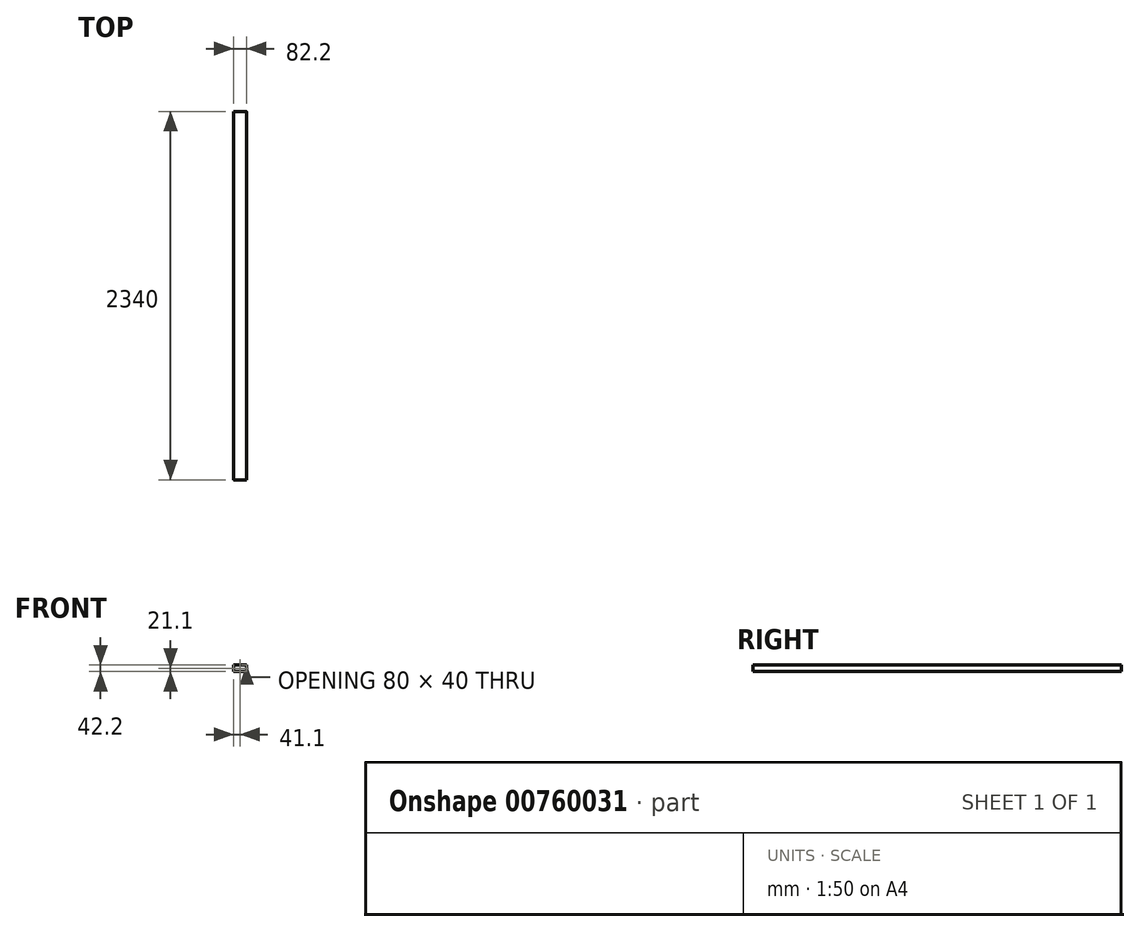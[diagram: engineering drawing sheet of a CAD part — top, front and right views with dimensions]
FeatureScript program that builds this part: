
annotation { "Feature Type Name" : "Feature", "Feature Type Description" : "" }
export const myFeature = defineFeature(function(context is Context, id is Id, definition is map)
    precondition{}
    {
        {
            assignVariable(context, id + "F0", {"name" : "LENGTH", "anyValue" : 2340});
        }
        {
            var Q0;
            Q0=qCreatedBy(makeId("Front.planeOp"),FACE);
            var sketch = newSketch(context, id + "F1", { "sketchPlane" : qUnion([Q0])});
            skLineSegment(sketch, "E0.bottom", {"start": v(-35, 20) * mm, "end": v(35, 20) * mm});
            skLineSegment(sketch, "E0.top", {"start": v(-35, -20) * mm, "end": v(35, -20) * mm});
            skLineSegment(sketch, "E0.left", {"start": v(-40, 15) * mm, "end": v(-40, -15) * mm});
            skLineSegment(sketch, "E0.right", {"start": v(40, 15) * mm, "end": v(40, -15) * mm});
            skPoint(sketch, "E1.visualSharp", {"position": v(-40, 20) * mm});
            skArc(sketch, "E1.filletArc", {"start": v(-35, 20) * mm, "mid": v(-38.54, 18.54) * mm, "end": v(-40, 15) * mm});
            skPoint(sketch, "E2.visualSharp", {"position": v(40, 20) * mm});
            skArc(sketch, "E2.filletArc", {"start": v(40, 15) * mm, "mid": v(38.54, 18.54) * mm, "end": v(35, 20) * mm});
            skPoint(sketch, "E3.visualSharp", {"position": v(40, -20) * mm});
            skArc(sketch, "E3.filletArc", {"start": v(35, -20) * mm, "mid": v(38.54, -18.54) * mm, "end": v(40, -15) * mm});
            skPoint(sketch, "E4.visualSharp", {"position": v(-40, -20) * mm});
            skArc(sketch, "E4.filletArc", {"start": v(-40, -15) * mm, "mid": v(-38.54, -18.54) * mm, "end": v(-35, -20) * mm});
            skLineSegment(sketch, "E5.0", {"start": v(41.1, 16.1) * mm, "end": v(41.1, -16.1) * mm});
            skLineSegment(sketch, "E5.1", {"start": v(-36.1, 21.1) * mm, "end": v(36.1, 21.1) * mm});
            skLineSegment(sketch, "E5.2", {"start": v(-41.1, 16.1) * mm, "end": v(-41.1, -16.1) * mm});
            skLineSegment(sketch, "E5.3", {"start": v(-36.1, -21.1) * mm, "end": v(36.1, -21.1) * mm});
            skPoint(sketch, "E6.visualSharp", {"position": v(-41.1, 21.1) * mm});
            skArc(sketch, "E6.filletArc", {"start": v(-36.1, 21.1) * mm, "mid": v(-39.64, 19.64) * mm, "end": v(-41.1, 16.1) * mm});
            skPoint(sketch, "E7.visualSharp", {"position": v(41.1, 21.1) * mm});
            skArc(sketch, "E7.filletArc", {"start": v(41.1, 16.1) * mm, "mid": v(39.64, 19.64) * mm, "end": v(36.1, 21.1) * mm});
            skPoint(sketch, "E8.visualSharp", {"position": v(41.1, -21.1) * mm});
            skArc(sketch, "E8.filletArc", {"start": v(36.1, -21.1) * mm, "mid": v(39.64, -19.64) * mm, "end": v(41.1, -16.1) * mm});
            skPoint(sketch, "E9.visualSharp", {"position": v(-41.1, -21.1) * mm});
            skArc(sketch, "E9.filletArc", {"start": v(-41.1, -16.1) * mm, "mid": v(-39.64, -19.64) * mm, "end": v(-36.1, -21.1) * mm});
            skSolve(sketch);
        }
        {
            var Q0;
            Q0=makeQuery(id+"F1.imprint","IMPRINT",FACE,{"disambiguationData":[TD([[makeQuery(id+"F1.imprint","IMPRINT",EDGE,{"derivedFrom":sQuery(id+"F1.wireOp",EDGE,"E0.bottom")}),1.0]])]});
            extrude(context, id + "F2", {"entities" : qUnion([Q0]), "depth" : (getVariable(context, 'LENGTH')) * mm, "offsetDistance" : 25 * mm});
        }
        {
            var Q0;
            Q0=qCreatedBy(makeId("Front.planeOp"),FACE);
            var sketch = newSketch(context, id + "F3", { "sketchPlane" : qUnion([Q0])});
            skPoint(sketch, "E10", {"position": v(0, 0) * mm});
            skSolve(sketch);
        }
        {
            var Q0;
            Q0=makeQuery(id+"F2.opExtrude","CAP_FACE",FACE,{"disambiguationData":[OSD([sQuery(id+"F1.wireOp",EDGE,"E0.bottom"),sQuery(id+"F1.wireOp",EDGE,"E0.top"),sQuery(id+"F1.wireOp",EDGE,"E0.left"),sQuery(id+"F1.wireOp",EDGE,"E0.right"),sQuery(id+"F1.wireOp",EDGE,"E1.filletArc"),sQuery(id+"F1.wireOp",EDGE,"E2.filletArc"),sQuery(id+"F1.wireOp",EDGE,"E3.filletArc"),sQuery(id+"F1.wireOp",EDGE,"E4.filletArc"),sQuery(id+"F1.wireOp",EDGE,"E5.0"),sQuery(id+"F1.wireOp",EDGE,"E5.1"),sQuery(id+"F1.wireOp",EDGE,"E5.2"),sQuery(id+"F1.wireOp",EDGE,"E5.3"),sQuery(id+"F1.wireOp",EDGE,"E6.filletArc"),sQuery(id+"F1.wireOp",EDGE,"E7.filletArc"),sQuery(id+"F1.wireOp",EDGE,"E8.filletArc"),sQuery(id+"F1.wireOp",EDGE,"E9.filletArc")])],"isStart":false});
            var sketch = newSketch(context, id + "F4", { "sketchPlane" : qUnion([Q0])});
            skPoint(sketch, "E11", {"position": v(0, 0) * mm});
            skSolve(sketch);
        }
    });
